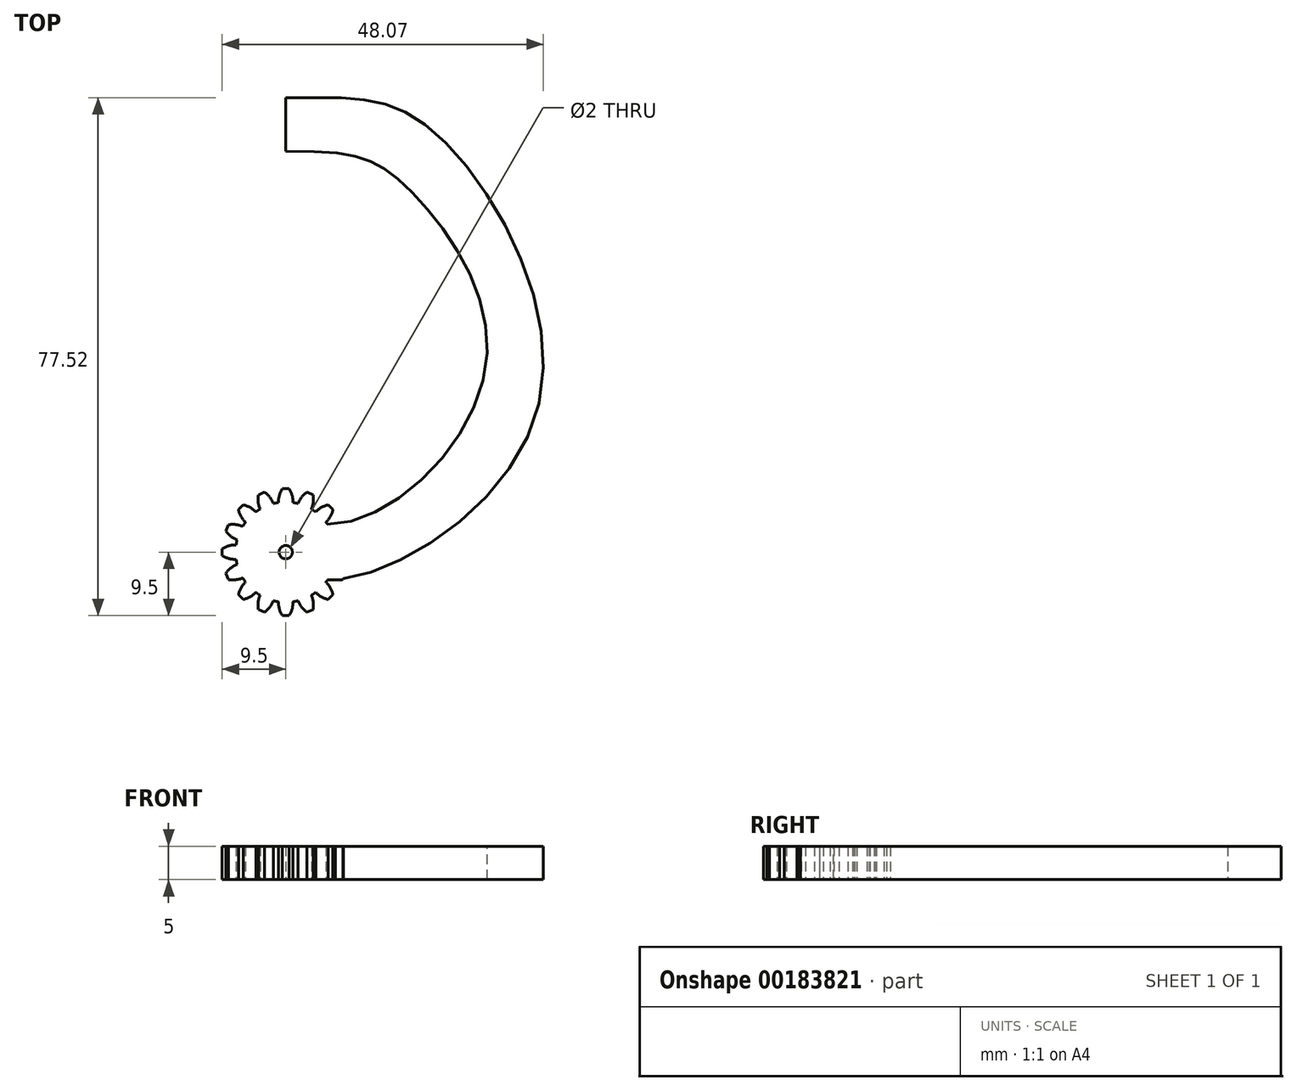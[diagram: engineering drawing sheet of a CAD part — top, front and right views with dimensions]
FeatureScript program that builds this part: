
annotation { "Feature Type Name" : "Feature", "Feature Type Description" : "" }
export const myFeature = defineFeature(function(context is Context, id is Id, definition is map)
    precondition{}
    {
        {
            var Q0;
            Q0=qCreatedBy(makeId("Top.planeOp"),FACE);
            var sketch = newSketch(context, id + "F0", { "sketchPlane" : qUnion([Q0])});
            skCircle(sketch, "E0", {"center": v(0, 0) * mm, "radius": 7.5 * mm});
            skLineSegment(sketch, "E1", {"start": v(0, 0) * mm, "end": v(0, 7.5) * mm, "construction": true});
            skArc(sketch, "E2", {"start": v(-0.5, 9.5) * mm, "mid": v(-0.95, 8.5) * mm, "end": v(-1.09, 7.42) * mm});
            skLineSegment(sketch, "E3", {"start": v(0, 9.5) * mm, "end": v(-0.5, 9.5) * mm});
            skLineSegment(sketch, "E4.MirrorCS", {"start": v(0, 9.5) * mm, "end": v(0.5, 9.5) * mm});
            skArc(sketch, "E5.MirrorCS", {"start": v(0.5, 9.5) * mm, "mid": v(0.95, 8.5) * mm, "end": v(1.09, 7.42) * mm});
            skArc(sketch, "E6.1.0", {"start": v(-3.17, 8.97) * mm, "mid": v(-2.38, 8.22) * mm, "end": v(-1.83, 7.27) * mm});
            skLineSegment(sketch, "E6.1.1", {"start": v(-3.64, 8.78) * mm, "end": v(-3.17, 8.97) * mm});
            skLineSegment(sketch, "E6.1.2", {"start": v(-3.64, 8.78) * mm, "end": v(-4.1, 8.59) * mm});
            skArc(sketch, "E6.1.3", {"start": v(-4.1, 8.59) * mm, "mid": v(-4.13, 7.5) * mm, "end": v(-3.85, 6.44) * mm});
            skArc(sketch, "E6.2.0", {"start": v(-6.36, 7.07) * mm, "mid": v(-5.34, 6.69) * mm, "end": v(-4.48, 6.02) * mm});
            skLineSegment(sketch, "E6.2.1", {"start": v(-6.72, 6.72) * mm, "end": v(-6.36, 7.07) * mm});
            skLineSegment(sketch, "E6.2.2", {"start": v(-6.72, 6.72) * mm, "end": v(-7.07, 6.36) * mm});
            skArc(sketch, "E6.2.3", {"start": v(-7.07, 6.36) * mm, "mid": v(-6.69, 5.34) * mm, "end": v(-6.02, 4.48) * mm});
            skArc(sketch, "E6.3.0", {"start": v(-8.59, 4.1) * mm, "mid": v(-7.5, 4.13) * mm, "end": v(-6.44, 3.85) * mm});
            skLineSegment(sketch, "E6.3.1", {"start": v(-8.78, 3.64) * mm, "end": v(-8.59, 4.1) * mm});
            skLineSegment(sketch, "E6.3.2", {"start": v(-8.78, 3.64) * mm, "end": v(-8.97, 3.17) * mm});
            skArc(sketch, "E6.3.3", {"start": v(-8.97, 3.17) * mm, "mid": v(-8.22, 2.38) * mm, "end": v(-7.27, 1.83) * mm});
            skArc(sketch, "E6.4.0", {"start": v(-9.5, 0.5) * mm, "mid": v(-8.5, 0.95) * mm, "end": v(-7.42, 1.09) * mm});
            skLineSegment(sketch, "E6.4.1", {"start": v(-9.5, 0) * mm, "end": v(-9.5, 0.5) * mm});
            skLineSegment(sketch, "E6.4.2", {"start": v(-9.5, 0) * mm, "end": v(-9.5, -0.5) * mm});
            skArc(sketch, "E6.4.3", {"start": v(-9.5, -0.5) * mm, "mid": v(-8.5, -0.95) * mm, "end": v(-7.42, -1.09) * mm});
            skArc(sketch, "E6.5.0", {"start": v(-8.97, -3.17) * mm, "mid": v(-8.22, -2.38) * mm, "end": v(-7.27, -1.83) * mm});
            skLineSegment(sketch, "E6.5.1", {"start": v(-8.78, -3.64) * mm, "end": v(-8.97, -3.17) * mm});
            skLineSegment(sketch, "E6.5.2", {"start": v(-8.78, -3.64) * mm, "end": v(-8.59, -4.1) * mm});
            skArc(sketch, "E6.5.3", {"start": v(-8.59, -4.1) * mm, "mid": v(-7.5, -4.13) * mm, "end": v(-6.44, -3.85) * mm});
            skArc(sketch, "E6.6.0", {"start": v(-7.07, -6.36) * mm, "mid": v(-6.69, -5.34) * mm, "end": v(-6.02, -4.48) * mm});
            skLineSegment(sketch, "E6.6.1", {"start": v(-6.72, -6.72) * mm, "end": v(-7.07, -6.36) * mm});
            skLineSegment(sketch, "E6.6.2", {"start": v(-6.72, -6.72) * mm, "end": v(-6.36, -7.07) * mm});
            skArc(sketch, "E6.6.3", {"start": v(-6.36, -7.07) * mm, "mid": v(-5.34, -6.69) * mm, "end": v(-4.48, -6.02) * mm});
            skArc(sketch, "E6.7.0", {"start": v(-4.1, -8.59) * mm, "mid": v(-4.13, -7.5) * mm, "end": v(-3.85, -6.44) * mm});
            skLineSegment(sketch, "E6.7.1", {"start": v(-3.64, -8.78) * mm, "end": v(-4.1, -8.59) * mm});
            skLineSegment(sketch, "E6.7.2", {"start": v(-3.64, -8.78) * mm, "end": v(-3.17, -8.97) * mm});
            skArc(sketch, "E6.7.3", {"start": v(-3.17, -8.97) * mm, "mid": v(-2.38, -8.22) * mm, "end": v(-1.83, -7.27) * mm});
            skArc(sketch, "E6.8.0", {"start": v(-0.5, -9.5) * mm, "mid": v(-0.95, -8.5) * mm, "end": v(-1.09, -7.42) * mm});
            skLineSegment(sketch, "E6.8.1", {"start": v(0, -9.5) * mm, "end": v(-0.5, -9.5) * mm});
            skLineSegment(sketch, "E6.8.2", {"start": v(0, -9.5) * mm, "end": v(0.5, -9.5) * mm});
            skArc(sketch, "E6.8.3", {"start": v(0.5, -9.5) * mm, "mid": v(0.95, -8.5) * mm, "end": v(1.09, -7.42) * mm});
            skArc(sketch, "E6.9.0", {"start": v(3.17, -8.97) * mm, "mid": v(2.38, -8.22) * mm, "end": v(1.83, -7.27) * mm});
            skLineSegment(sketch, "E6.9.1", {"start": v(3.64, -8.78) * mm, "end": v(3.17, -8.97) * mm});
            skLineSegment(sketch, "E6.9.2", {"start": v(3.64, -8.78) * mm, "end": v(4.1, -8.59) * mm});
            skArc(sketch, "E6.9.3", {"start": v(4.1, -8.59) * mm, "mid": v(4.13, -7.5) * mm, "end": v(3.85, -6.44) * mm});
            skArc(sketch, "E6.10.0", {"start": v(6.36, -7.07) * mm, "mid": v(5.34, -6.69) * mm, "end": v(4.48, -6.02) * mm});
            skLineSegment(sketch, "E6.10.1", {"start": v(6.72, -6.72) * mm, "end": v(6.36, -7.07) * mm});
            skLineSegment(sketch, "E6.10.2", {"start": v(6.72, -6.72) * mm, "end": v(7.07, -6.36) * mm});
            skArc(sketch, "E6.10.3", {"start": v(7.07, -6.36) * mm, "mid": v(6.69, -5.34) * mm, "end": v(6.02, -4.48) * mm});
            skArc(sketch, "E6.11.0", {"start": v(8.59, -4.1) * mm, "mid": v(7.5, -4.13) * mm, "end": v(6.44, -3.85) * mm});
            skLineSegment(sketch, "E6.11.1", {"start": v(8.78, -3.64) * mm, "end": v(8.59, -4.1) * mm});
            skLineSegment(sketch, "E6.11.2", {"start": v(8.78, -3.64) * mm, "end": v(8.97, -3.17) * mm});
            skArc(sketch, "E6.11.3", {"start": v(8.97, -3.17) * mm, "mid": v(8.22, -2.38) * mm, "end": v(7.27, -1.83) * mm});
            skArc(sketch, "E6.12.0", {"start": v(9.5, -0.5) * mm, "mid": v(8.5, -0.95) * mm, "end": v(7.42, -1.09) * mm});
            skLineSegment(sketch, "E6.12.1", {"start": v(9.5, 0) * mm, "end": v(9.5, -0.5) * mm});
            skLineSegment(sketch, "E6.12.2", {"start": v(9.5, 0) * mm, "end": v(9.5, 0.5) * mm});
            skArc(sketch, "E6.12.3", {"start": v(9.5, 0.5) * mm, "mid": v(8.5, 0.95) * mm, "end": v(7.42, 1.09) * mm});
            skArc(sketch, "E6.13.0", {"start": v(8.97, 3.17) * mm, "mid": v(8.22, 2.38) * mm, "end": v(7.27, 1.83) * mm});
            skLineSegment(sketch, "E6.13.1", {"start": v(8.78, 3.64) * mm, "end": v(8.97, 3.17) * mm});
            skLineSegment(sketch, "E6.13.2", {"start": v(8.78, 3.64) * mm, "end": v(8.59, 4.1) * mm});
            skArc(sketch, "E6.13.3", {"start": v(8.59, 4.1) * mm, "mid": v(7.5, 4.13) * mm, "end": v(6.44, 3.85) * mm});
            skArc(sketch, "E6.14.0", {"start": v(7.07, 6.36) * mm, "mid": v(6.69, 5.34) * mm, "end": v(6.02, 4.48) * mm});
            skLineSegment(sketch, "E6.14.1", {"start": v(6.72, 6.72) * mm, "end": v(7.07, 6.36) * mm});
            skLineSegment(sketch, "E6.14.2", {"start": v(6.72, 6.72) * mm, "end": v(6.36, 7.07) * mm});
            skArc(sketch, "E6.14.3", {"start": v(6.36, 7.07) * mm, "mid": v(5.34, 6.69) * mm, "end": v(4.48, 6.02) * mm});
            skArc(sketch, "E6.15.0", {"start": v(4.1, 8.59) * mm, "mid": v(4.13, 7.5) * mm, "end": v(3.85, 6.44) * mm});
            skLineSegment(sketch, "E6.15.1", {"start": v(3.64, 8.78) * mm, "end": v(4.1, 8.59) * mm});
            skLineSegment(sketch, "E6.15.2", {"start": v(3.64, 8.78) * mm, "end": v(3.17, 8.97) * mm});
            skArc(sketch, "E6.15.3", {"start": v(3.17, 8.97) * mm, "mid": v(2.38, 8.22) * mm, "end": v(1.83, 7.27) * mm});
            skSolve(sketch);
        }
        {
            var Q0;
            Q0=qSketchRegion(id+"F0",true);
            extrude(context, id + "F1", {"entities" : qUnion([Q0]), "depth" : 5 * mm});
        }
        {
            var Q0;
            Q0=makeQuery(id+"F1.opExtrude","CAP_FACE",FACE,{"disambiguationData":[OSD([sQuery(id+"F0.wireOp",EDGE,"E0"),sQuery(id+"F0.wireOp",EDGE,"E2"),sQuery(id+"F0.wireOp",EDGE,"E3"),sQuery(id+"F0.wireOp",EDGE,"E4.MirrorCS"),sQuery(id+"F0.wireOp",EDGE,"E5.MirrorCS"),sQuery(id+"F0.wireOp",EDGE,"E6.1.0"),sQuery(id+"F0.wireOp",EDGE,"E6.1.1"),sQuery(id+"F0.wireOp",EDGE,"E6.1.2"),sQuery(id+"F0.wireOp",EDGE,"E6.1.3"),sQuery(id+"F0.wireOp",EDGE,"E6.2.0"),sQuery(id+"F0.wireOp",EDGE,"E6.2.1"),sQuery(id+"F0.wireOp",EDGE,"E6.2.2"),sQuery(id+"F0.wireOp",EDGE,"E6.2.3"),sQuery(id+"F0.wireOp",EDGE,"E6.3.0"),sQuery(id+"F0.wireOp",EDGE,"E6.3.1"),sQuery(id+"F0.wireOp",EDGE,"E6.3.2"),sQuery(id+"F0.wireOp",EDGE,"E6.3.3"),sQuery(id+"F0.wireOp",EDGE,"E6.4.0"),sQuery(id+"F0.wireOp",EDGE,"E6.4.1"),sQuery(id+"F0.wireOp",EDGE,"E6.4.2"),sQuery(id+"F0.wireOp",EDGE,"E6.4.3"),sQuery(id+"F0.wireOp",EDGE,"E6.5.0"),sQuery(id+"F0.wireOp",EDGE,"E6.5.1"),sQuery(id+"F0.wireOp",EDGE,"E6.5.2"),sQuery(id+"F0.wireOp",EDGE,"E6.5.3"),sQuery(id+"F0.wireOp",EDGE,"E6.6.0"),sQuery(id+"F0.wireOp",EDGE,"E6.6.1"),sQuery(id+"F0.wireOp",EDGE,"E6.6.2"),sQuery(id+"F0.wireOp",EDGE,"E6.6.3"),sQuery(id+"F0.wireOp",EDGE,"E6.7.0"),sQuery(id+"F0.wireOp",EDGE,"E6.7.1"),sQuery(id+"F0.wireOp",EDGE,"E6.7.2"),sQuery(id+"F0.wireOp",EDGE,"E6.7.3"),sQuery(id+"F0.wireOp",EDGE,"E6.8.0"),sQuery(id+"F0.wireOp",EDGE,"E6.8.1"),sQuery(id+"F0.wireOp",EDGE,"E6.8.2"),sQuery(id+"F0.wireOp",EDGE,"E6.8.3"),sQuery(id+"F0.wireOp",EDGE,"E6.9.0"),sQuery(id+"F0.wireOp",EDGE,"E6.9.1"),sQuery(id+"F0.wireOp",EDGE,"E6.9.2"),sQuery(id+"F0.wireOp",EDGE,"E6.9.3"),sQuery(id+"F0.wireOp",EDGE,"E6.10.0"),sQuery(id+"F0.wireOp",EDGE,"E6.10.1"),sQuery(id+"F0.wireOp",EDGE,"E6.10.2"),sQuery(id+"F0.wireOp",EDGE,"E6.10.3"),sQuery(id+"F0.wireOp",EDGE,"E6.11.0"),sQuery(id+"F0.wireOp",EDGE,"E6.11.1"),sQuery(id+"F0.wireOp",EDGE,"E6.11.2"),sQuery(id+"F0.wireOp",EDGE,"E6.11.3"),sQuery(id+"F0.wireOp",EDGE,"E6.12.0"),sQuery(id+"F0.wireOp",EDGE,"E6.12.1"),sQuery(id+"F0.wireOp",EDGE,"E6.12.2"),sQuery(id+"F0.wireOp",EDGE,"E6.12.3"),sQuery(id+"F0.wireOp",EDGE,"E6.13.0"),sQuery(id+"F0.wireOp",EDGE,"E6.13.1"),sQuery(id+"F0.wireOp",EDGE,"E6.13.2"),sQuery(id+"F0.wireOp",EDGE,"E6.13.3"),sQuery(id+"F0.wireOp",EDGE,"E6.14.0"),sQuery(id+"F0.wireOp",EDGE,"E6.14.1"),sQuery(id+"F0.wireOp",EDGE,"E6.14.2"),sQuery(id+"F0.wireOp",EDGE,"E6.14.3"),sQuery(id+"F0.wireOp",EDGE,"E6.15.0"),sQuery(id+"F0.wireOp",EDGE,"E6.15.1"),sQuery(id+"F0.wireOp",EDGE,"E6.15.2"),sQuery(id+"F0.wireOp",EDGE,"E6.15.3")])],"isStart":false});
            var sketch = newSketch(context, id + "F2", { "sketchPlane" : qUnion([Q0])});
            skCircle(sketch, "E7", {"center": v(0, 0) * mm, "radius": 1 * mm});
            skSolve(sketch);
        }
        {
            var Q0;
            Q0=qSketchRegion(id+"F2",true);
            extrude(context, id + "F3", {"entities" : qUnion([Q0]), "operationType" : NewBodyOperationType.REMOVE, "oppositeDirection" : true, "depth" : 25 * mm});
        }
        {
            var Q0;
            Q0=qCreatedBy(makeId("Top.planeOp"),FACE);
            var sketch = newSketch(context, id + "F4", { "sketchPlane" : qUnion([Q0])});
            skLineSegment(sketch, "E8", {"start": v(0, 68) * mm, "end": v(0, 60) * mm});
            skFitSpline(sketch, "E9", {"points": [v(0, 60) * mm, v(17.35, 55.31) * mm, v(30.02, 28.29) * mm, v(6.24, 4.17) * mm], "startDerivative": vector(109.86, 0) * mm, "endDerivative": vector(-80.01, 0) * mm});
            skFitSpline(sketch, "E10", {"points": [v(0, 68) * mm, v(21.63, 63.35) * mm, v(37.7, 21.4) * mm, v(6.24, -4.17) * mm], "startDerivative": vector(113.37, 0) * mm, "endDerivative": vector(-83.73, 0) * mm});
            skLineSegment(sketch, "E11", {"start": v(6.24, 4.17) * mm, "end": v(6.24, -4.17) * mm});
            skSolve(sketch);
        }
        {
            var Q0;
            Q0 = qSketchRegion(id + "F4", true);
            var Q1;
            Q1=makeQuery(id+"F1.opExtrude","CAP_FACE",FACE,{"disambiguationData":[OSD([sQuery(id+"F0.wireOp",EDGE,"E0"),sQuery(id+"F0.wireOp",EDGE,"E2"),sQuery(id+"F0.wireOp",EDGE,"E3"),sQuery(id+"F0.wireOp",EDGE,"E4.MirrorCS"),sQuery(id+"F0.wireOp",EDGE,"E5.MirrorCS"),sQuery(id+"F0.wireOp",EDGE,"E6.1.0"),sQuery(id+"F0.wireOp",EDGE,"E6.1.1"),sQuery(id+"F0.wireOp",EDGE,"E6.1.2"),sQuery(id+"F0.wireOp",EDGE,"E6.1.3"),sQuery(id+"F0.wireOp",EDGE,"E6.2.0"),sQuery(id+"F0.wireOp",EDGE,"E6.2.1"),sQuery(id+"F0.wireOp",EDGE,"E6.2.2"),sQuery(id+"F0.wireOp",EDGE,"E6.2.3"),sQuery(id+"F0.wireOp",EDGE,"E6.3.0"),sQuery(id+"F0.wireOp",EDGE,"E6.3.1"),sQuery(id+"F0.wireOp",EDGE,"E6.3.2"),sQuery(id+"F0.wireOp",EDGE,"E6.3.3"),sQuery(id+"F0.wireOp",EDGE,"E6.4.0"),sQuery(id+"F0.wireOp",EDGE,"E6.4.1"),sQuery(id+"F0.wireOp",EDGE,"E6.4.2"),sQuery(id+"F0.wireOp",EDGE,"E6.4.3"),sQuery(id+"F0.wireOp",EDGE,"E6.5.0"),sQuery(id+"F0.wireOp",EDGE,"E6.5.1"),sQuery(id+"F0.wireOp",EDGE,"E6.5.2"),sQuery(id+"F0.wireOp",EDGE,"E6.5.3"),sQuery(id+"F0.wireOp",EDGE,"E6.6.0"),sQuery(id+"F0.wireOp",EDGE,"E6.6.1"),sQuery(id+"F0.wireOp",EDGE,"E6.6.2"),sQuery(id+"F0.wireOp",EDGE,"E6.6.3"),sQuery(id+"F0.wireOp",EDGE,"E6.7.0"),sQuery(id+"F0.wireOp",EDGE,"E6.7.1"),sQuery(id+"F0.wireOp",EDGE,"E6.7.2"),sQuery(id+"F0.wireOp",EDGE,"E6.7.3"),sQuery(id+"F0.wireOp",EDGE,"E6.8.0"),sQuery(id+"F0.wireOp",EDGE,"E6.8.1"),sQuery(id+"F0.wireOp",EDGE,"E6.8.2"),sQuery(id+"F0.wireOp",EDGE,"E6.8.3"),sQuery(id+"F0.wireOp",EDGE,"E6.9.0"),sQuery(id+"F0.wireOp",EDGE,"E6.9.1"),sQuery(id+"F0.wireOp",EDGE,"E6.9.2"),sQuery(id+"F0.wireOp",EDGE,"E6.9.3"),sQuery(id+"F0.wireOp",EDGE,"E6.10.0"),sQuery(id+"F0.wireOp",EDGE,"E6.10.1"),sQuery(id+"F0.wireOp",EDGE,"E6.10.2"),sQuery(id+"F0.wireOp",EDGE,"E6.10.3"),sQuery(id+"F0.wireOp",EDGE,"E6.11.0"),sQuery(id+"F0.wireOp",EDGE,"E6.11.1"),sQuery(id+"F0.wireOp",EDGE,"E6.11.2"),sQuery(id+"F0.wireOp",EDGE,"E6.11.3"),sQuery(id+"F0.wireOp",EDGE,"E6.12.0"),sQuery(id+"F0.wireOp",EDGE,"E6.12.1"),sQuery(id+"F0.wireOp",EDGE,"E6.12.2"),sQuery(id+"F0.wireOp",EDGE,"E6.12.3"),sQuery(id+"F0.wireOp",EDGE,"E6.13.0"),sQuery(id+"F0.wireOp",EDGE,"E6.13.1"),sQuery(id+"F0.wireOp",EDGE,"E6.13.2"),sQuery(id+"F0.wireOp",EDGE,"E6.13.3"),sQuery(id+"F0.wireOp",EDGE,"E6.14.0"),sQuery(id+"F0.wireOp",EDGE,"E6.14.1"),sQuery(id+"F0.wireOp",EDGE,"E6.14.2"),sQuery(id+"F0.wireOp",EDGE,"E6.14.3"),sQuery(id+"F0.wireOp",EDGE,"E6.15.0"),sQuery(id+"F0.wireOp",EDGE,"E6.15.1"),sQuery(id+"F0.wireOp",EDGE,"E6.15.2"),sQuery(id+"F0.wireOp",EDGE,"E6.15.3")])],"isStart":false});
            extrude(context, id + "F5", {"entities" : qUnion([Q0]), "operationType" : NewBodyOperationType.ADD, "endBound" : BoundingType.UP_TO_SURFACE, "endBoundEntityFace" : qUnion([Q1]), "depth" : 25 * mm});
        }
    });
